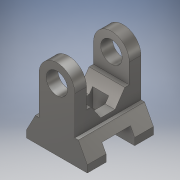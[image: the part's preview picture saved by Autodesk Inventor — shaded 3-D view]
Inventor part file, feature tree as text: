
AUTODESK INVENTOR PART (.ipt)
format: ipt  version: 2018 (Build 220112000, 112)  size: 177,664 bytes
history: native  units: mm
features: extrude x3, sketch x2
ambient origin geometry x8: Origin, YZ Plane, XZ Plane, XY Plane, X Axis, Y Axis, Z Axis, Center Point
bodies: Solid1 (feature_tree)
feature tree (5):
  sketch  "Sketch1"  dims[d0=70.0mm d1=24.0mm]
  extrude  "Extrusion1"  Depth=24.0mm
  extrude  "Extrusion2"  Depth=34.0mm
  extrude  "Extrusion3"  Depth=34.0mm
  sketch  "Sketch2"  dims[d2=20.0mm d3=34.0mm d4=34.0mm d5=8.0mm d6=8.0mm d10=4.0mm d11=4.0mm d14=19.0mm d15=19.0mm d16=74.0mm d17=0.0mm d23=32.0mm d24=16.0mm d27=38.0mm d32=84.0mm d33=0.0mm d34=17.0mm d35=9.0mm d39=18.0mm d43=24.0mm d44=0.0mm d45=32.0mm d46=17.0mm d47=13.0mm d48=13.0mm d49=5.0mm d50=16.0mm d58=11.0mm d69=48.0mm d70=21.0mm d72=56.0mm d73=74.0mm]
